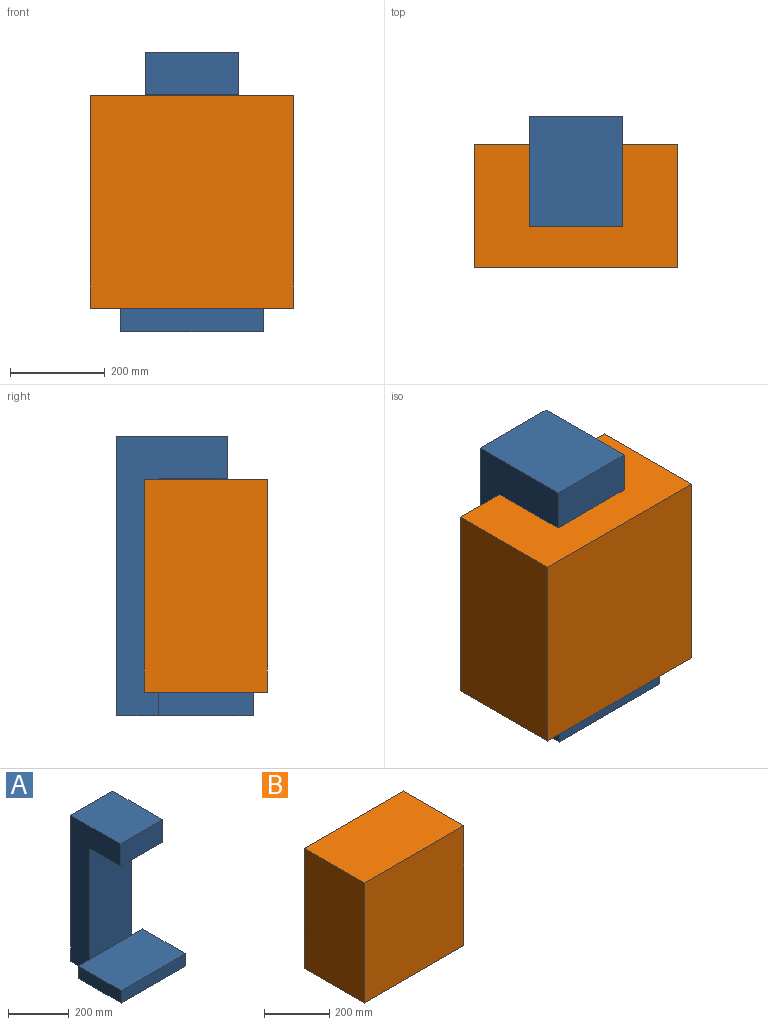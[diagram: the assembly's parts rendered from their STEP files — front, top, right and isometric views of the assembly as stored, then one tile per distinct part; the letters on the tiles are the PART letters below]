
ASSEMBLY  parts=2 mates=1
PART A: 14 faces, bbox 300x288x590 mm
  f0: plane 450x197mm, normal (0,-1,0), area 88650mm2, adj f6,f8,f9,f12
  f1: plane 51.5x50mm, normal (0,1,0), area 2575mm2, adj f4,f6,f7,f8
  f2: plane 200x50mm, normal (-1,0,0), area 10000mm2, adj f3,f5,f6,f7
  f3: plane 300x50mm, normal (0,-1,0), area 15000mm2, adj f2,f4,f6,f7
  f4: plane 200x50mm, normal (1,0,0), area 10000mm2, adj f1,f3,f6,f7
  f5: plane 51.5x50mm, normal (0,1,0), area 2575mm2, adj f2,f6,f7,f9
  f6: plane 300x200mm, normal (0,0,1), area 60000mm2, adj f0,f1,f2,f3,f4,f5
  f7: plane 300x288mm, normal (0,0,-1), area 77336mm2, adj f1,f2,f3,f4,f5,f8,f9,f11
  f8: plane 590x233mm, normal (1,0,0), area 64970mm2, adj f0,f1,f7,f10,f11,f12,f13
  f9: plane 590x233mm, normal (-1,0,0), area 64970mm2, adj f0,f5,f7,f10,f11,f12,f13
  f10: plane 233x197mm, normal (0,0,1), area 45901mm2, adj f8,f9,f11,f13
  f11: plane 590x197mm, normal (0,1,0), area 116230mm2, adj f7,f8,f9,f10
  f12: plane 197x145mm, normal (0,0,-1), area 28565mm2, adj f0,f8,f9,f13
  f13: plane 197x90mm, normal (0,-1,0), area 17730mm2, adj f8,f9,f10,f12
PART B: 6 faces, bbox 430x260x449 mm
  f0: plane 449x260mm, normal (1,0,0), area 116740mm2, adj f1,f3,f4,f5
  f1: plane 449x430mm, normal (0,1,0), area 193070mm2, adj f0,f2,f4,f5
  f2: plane 449x260mm, normal (-1,0,0), area 116740mm2, adj f1,f3,f4,f5
  f3: plane 449x430mm, normal (0,-1,0), area 193070mm2, adj f0,f2,f4,f5
  f4: plane 430x260mm, normal (0,0,1), area 111800mm2, adj f0,f1,f2,f3
  f5: plane 430x260mm, normal (0,0,-1), area 111800mm2, adj f0,f1,f2,f3
PLACE A t=(-979.28,644.95,-359.81)mm
PLACE B t=(-979.28,674.95,-359.81)mm
MATE revolute B.f5 <-> A.f6  axis (0,0,-1) through (-829.28,744.95,-309.81)mm
